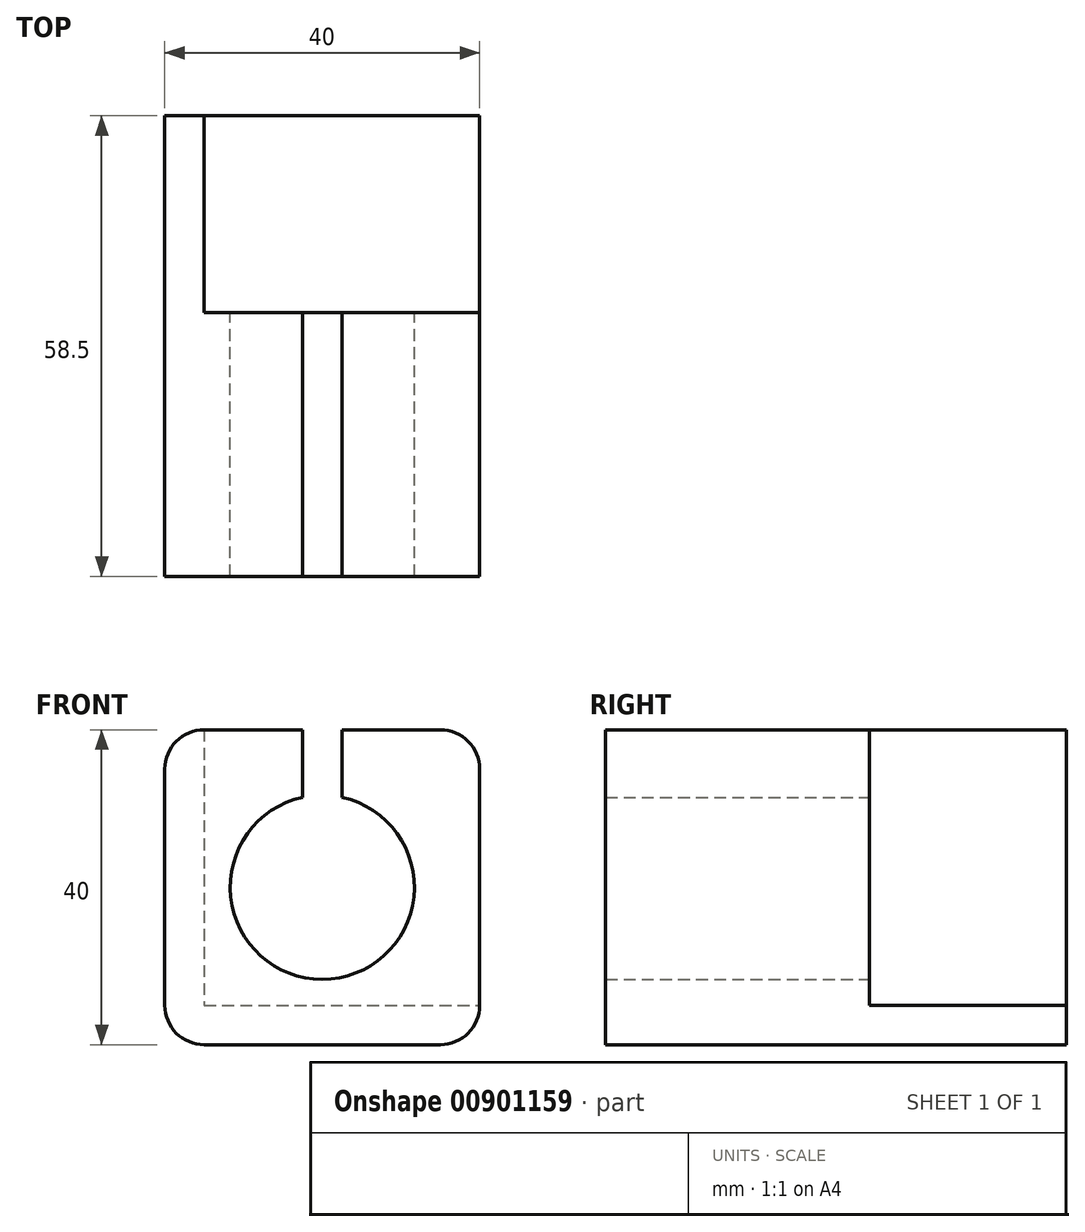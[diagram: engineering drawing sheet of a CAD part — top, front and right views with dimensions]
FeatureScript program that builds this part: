
annotation { "Feature Type Name" : "Feature", "Feature Type Description" : "" }
export const myFeature = defineFeature(function(context is Context, id is Id, definition is map)
    precondition{}
    {
        {
            var Q0;
            Q0=qCreatedBy(makeId("Front.planeOp"),FACE);
            var sketch = newSketch(context, id + "F0", { "sketchPlane" : qUnion([Q0])});
            skLineSegment(sketch, "E0.bottom", {"start": v(20, 20) * mm, "end": v(-20, 20) * mm});
            skLineSegment(sketch, "E0.top", {"start": v(20, -20) * mm, "end": v(-20, -20) * mm});
            skLineSegment(sketch, "E0.left", {"start": v(20, 20) * mm, "end": v(20, -20) * mm});
            skLineSegment(sketch, "E0.right", {"start": v(-20, 20) * mm, "end": v(-20, -20) * mm});
            skPoint(sketch, "E0.middle", {"position": v(0, 0) * mm});
            skCircle(sketch, "E1", {"center": v(0, 0) * mm, "radius": 11.7 * mm});
            skSolve(sketch);
        }
        {
            var Q0;
            Q0 = qSketchRegion(id + "F0", true);
            extrude(context, id + "F1", {"entities" : qUnion([Q0]), "depth" : 3.5 * mm, "offsetDistance" : 25 * mm});
        }
        {
            var Q0;
            Q0=makeQuery(id+"F1.opExtrude","CAP_FACE",FACE,{"disambiguationData":[OSD([sQuery(id+"F0.wireOp",EDGE,"E0.bottom"),sQuery(id+"F0.wireOp",EDGE,"E0.top"),sQuery(id+"F0.wireOp",EDGE,"E0.left"),sQuery(id+"F0.wireOp",EDGE,"E0.right"),sQuery(id+"F0.wireOp",EDGE,"E1")])],"isStart":false});
            var sketch = newSketch(context, id + "F2", { "sketchPlane" : qUnion([Q0])});
            skCircle(sketch, "E2", {"center": v(0, 0) * mm, "radius": 11.7 * mm});
            skCircle(sketch, "E3.0", {"center": v(0, 0) * mm, "radius": 16.7 * mm});
            skSolve(sketch);
        }
        {
            var Q0;
            Q0 = qSketchRegion(id + "F2", true);
            extrude(context, id + "F3", {"entities" : qUnion([Q0]), "operationType" : NewBodyOperationType.ADD, "depth" : 30 * mm, "offsetDistance" : 25 * mm});
        }
        {
            var Q0;
            Q0=makeQuery(id+"F3.opExtrude","CAP_FACE",FACE,{"disambiguationData":[OSD([sQuery(id+"F2.wireOp",EDGE,"E2"),sQuery(id+"F2.wireOp",EDGE,"E3.0")])],"isStart":false});
            var sketch = newSketch(context, id + "F4", { "sketchPlane" : qUnion([Q0])});
            skLineSegment(sketch, "E4.0", {"start": v(2.5, 0) * mm, "end": v(2.5, 29.24) * mm});
            skLineSegment(sketch, "E5.0", {"start": v(-2.5, 0) * mm, "end": v(-2.5, 29.24) * mm});
            skLineSegment(sketch, "E6", {"start": v(2.5, 29.24) * mm, "end": v(-2.5, 29.24) * mm});
            skLineSegment(sketch, "E7", {"start": v(2.5, 0) * mm, "end": v(-2.5, 0) * mm});
            skPoint(sketch, "E8.orphan", {"position": v(0, 29.24) * mm});
            skSolve(sketch);
        }
        {
            var Q0;
            Q0 = qSketchRegion(id + "F4", true);
            var Q1;
            Q1=makeQuery(id+"F1.opExtrude","CAP_FACE",FACE,{"disambiguationData":[OSD([sQuery(id+"F0.wireOp",EDGE,"E0.bottom"),sQuery(id+"F0.wireOp",EDGE,"E0.top"),sQuery(id+"F0.wireOp",EDGE,"E0.left"),sQuery(id+"F0.wireOp",EDGE,"E0.right"),sQuery(id+"F0.wireOp",EDGE,"E1")])],"isStart":false});
            extrude(context, id + "F5", {"entities" : qUnion([Q0]), "operationType" : NewBodyOperationType.REMOVE, "endBound" : BoundingType.UP_TO_NEXT, "oppositeDirection" : true, "depth" : 25 * mm, "endBoundEntityFace" : qUnion([Q1]), "offsetDistance" : 25 * mm});
        }
        {
            var Q0;
            Q0=makeQuery(id+"F3.opExtrude","CAP_FACE",FACE,{"disambiguationData":[OSD([sQuery(id+"F2.wireOp",EDGE,"E2"),sQuery(id+"F2.wireOp",EDGE,"E3.0")])],"isStart":false});
            var sketch = newSketch(context, id + "F6", { "sketchPlane" : qUnion([Q0])});
            skCircle(sketch, "E9", {"center": v(0, 0) * mm, "radius": 16.7 * mm});
            skLineSegment(sketch, "E10.bottom", {"start": v(20, 20) * mm, "end": v(-20, 20) * mm});
            skLineSegment(sketch, "E10.top", {"start": v(20, -20) * mm, "end": v(-20, -20) * mm});
            skLineSegment(sketch, "E10.left", {"start": v(20, 20) * mm, "end": v(20, -20) * mm});
            skLineSegment(sketch, "E10.right", {"start": v(-20, 20) * mm, "end": v(-20, -20) * mm});
            skSolve(sketch);
        }
        {
            var Q0;
            Q0 = qSketchRegion(id + "F6", true);
            var Q1;
            Q1=makeQuery(id+"F1.opExtrude","SWEPT_BODY",BODY,{"disambiguationData":[OSD([sQuery(id+"F0.wireOp",EDGE,"E0.bottom"),sQuery(id+"F0.wireOp",EDGE,"E0.top"),sQuery(id+"F0.wireOp",EDGE,"E0.left"),sQuery(id+"F0.wireOp",EDGE,"E0.right"),sQuery(id+"F0.wireOp",EDGE,"E1")])]});
            extrude(context, id + "F7", {"entities" : qUnion([Q0]), "operationType" : NewBodyOperationType.ADD, "oppositeDirection" : true, "depth" : 30.5 * mm, "endBoundEntityBody" : qUnion([Q1]), "offsetDistance" : 25 * mm});
        }
        {
            var Q0;
            Q0=makeQuery(id+"F7.boolean.opBoolean","MERGE",FACE,{"derivedFrom":[makeQuery(id+"F3.opExtrude","CAP_FACE",FACE,{"disambiguationData":[OSD([sQuery(id+"F2.wireOp",EDGE,"E2"),sQuery(id+"F2.wireOp",EDGE,"E3.0")])],"isStart":false}),makeQuery(id+"F7.opExtrude","CAP_FACE",FACE,{"disambiguationData":[OSD([sQuery(id+"F6.wireOp",EDGE,"E9"),sQuery(id+"F6.wireOp",EDGE,"E10.bottom"),sQuery(id+"F6.wireOp",EDGE,"E10.top"),sQuery(id+"F6.wireOp",EDGE,"E10.left"),sQuery(id+"F6.wireOp",EDGE,"E10.right")])],"isStart":true})]});
            var sketch = newSketch(context, id + "F8", { "sketchPlane" : qUnion([Q0])});
            skLineSegment(sketch, "E11", {"start": v(2.5, 11.43) * mm, "end": v(2.5, 21.55) * mm});
            skLineSegment(sketch, "E12", {"start": v(2.5, 21.55) * mm, "end": v(-2.5, 21.55) * mm});
            skLineSegment(sketch, "E13", {"start": v(-2.5, 21.55) * mm, "end": v(-2.5, 7.93) * mm});
            skLineSegment(sketch, "E14", {"start": v(-2.5, 7.93) * mm, "end": v(2.5, 7.93) * mm});
            skLineSegment(sketch, "E15", {"start": v(2.5, 7.93) * mm, "end": v(2.5, 11.43) * mm});
            skSolve(sketch);
        }
        {
            var Q0;
            Q0 = qSketchRegion(id + "F8", true);
            extrude(context, id + "F9", {"entities" : qUnion([Q0]), "operationType" : NewBodyOperationType.REMOVE, "oppositeDirection" : true, "depth" : 37.3 * mm, "offsetDistance" : 25 * mm});
        }
        {
            var Q0;
            Q0=makeQuery(id+"F1.opExtrude","CAP_FACE",FACE,{"disambiguationData":[OSD([sQuery(id+"F0.wireOp",EDGE,"E0.bottom"),sQuery(id+"F0.wireOp",EDGE,"E0.top"),sQuery(id+"F0.wireOp",EDGE,"E0.left"),sQuery(id+"F0.wireOp",EDGE,"E0.right"),sQuery(id+"F0.wireOp",EDGE,"E1")])],"isStart":true});
            var sketch = newSketch(context, id + "F10", { "sketchPlane" : qUnion([Q0])});
            skLineSegment(sketch, "E16", {"start": v(20, 20) * mm, "end": v(20, -20) * mm});
            skLineSegment(sketch, "E17", {"start": v(20, -20) * mm, "end": v(-20, -20) * mm});
            skLineSegment(sketch, "E18.0", {"start": v(15, -15) * mm, "end": v(-20, -15) * mm});
            skLineSegment(sketch, "E18.1", {"start": v(15, 20) * mm, "end": v(15, -15) * mm});
            skLineSegment(sketch, "E19", {"start": v(-20, -20) * mm, "end": v(-20, -15) * mm});
            skLineSegment(sketch, "E20", {"start": v(20, 20) * mm, "end": v(15, 20) * mm});
            skSolve(sketch);
        }
        {
            var Q0;
            Q0 = qSketchRegion(id + "F10", true);
            extrude(context, id + "F11", {"entities" : qUnion([Q0]), "operationType" : NewBodyOperationType.ADD, "depth" : 25 * mm, "offsetDistance" : 25 * mm});
        }
        {
            var Q0;
            Q0=makeQuery(id+"F11.boolean.opBoolean","MERGE",EDGE,{"derivedFrom":[makeQuery(id+"F7.boolean.opBoolean","MERGE",EDGE,{"derivedFrom":[makeQuery(id+"F1.opExtrude","SWEPT_EDGE",EDGE,{"disambiguationData":[OSD([sQuery(id+"F0.wireOp",EDGE,"E0.top"),sQuery(id+"F0.wireOp",EDGE,"E0.right")])]}),makeQuery(id+"F7.opExtrude","SWEPT_EDGE",EDGE,{"disambiguationData":[OSD([sQuery(id+"F6.wireOp",EDGE,"E10.top"),sQuery(id+"F6.wireOp",EDGE,"E10.right")])]})]}),makeQuery(id+"F11.opExtrude","SWEPT_EDGE",EDGE,{"disambiguationData":[OSD([sQuery(id+"F10.wireOp",EDGE,"E16"),sQuery(id+"F10.wireOp",EDGE,"E17")])]})]});
            var Q1;
            Q1=makeQuery(id+"F11.boolean.opBoolean","MERGE",EDGE,{"derivedFrom":[makeQuery(id+"F7.boolean.opBoolean","MERGE",EDGE,{"derivedFrom":[makeQuery(id+"F1.opExtrude","SWEPT_EDGE",EDGE,{"disambiguationData":[OSD([sQuery(id+"F0.wireOp",EDGE,"E0.bottom"),sQuery(id+"F0.wireOp",EDGE,"E0.right")])]}),makeQuery(id+"F7.opExtrude","SWEPT_EDGE",EDGE,{"disambiguationData":[OSD([sQuery(id+"F6.wireOp",EDGE,"E10.bottom"),sQuery(id+"F6.wireOp",EDGE,"E10.right")])]})]}),makeQuery(id+"F11.opExtrude","SWEPT_EDGE",EDGE,{"disambiguationData":[OSD([sQuery(id+"F10.wireOp",EDGE,"E16"),sQuery(id+"F10.wireOp",EDGE,"E20")])]})]});
            var Q2;
            Q2=makeQuery(id+"F11.boolean.opBoolean","MERGE",EDGE,{"derivedFrom":[makeQuery(id+"F7.boolean.opBoolean","MERGE",EDGE,{"derivedFrom":[makeQuery(id+"F1.opExtrude","SWEPT_EDGE",EDGE,{"disambiguationData":[OSD([sQuery(id+"F0.wireOp",EDGE,"E0.top"),sQuery(id+"F0.wireOp",EDGE,"E0.left")])]}),makeQuery(id+"F7.opExtrude","SWEPT_EDGE",EDGE,{"disambiguationData":[OSD([sQuery(id+"F6.wireOp",EDGE,"E10.top"),sQuery(id+"F6.wireOp",EDGE,"E10.left")])]})]}),makeQuery(id+"F11.opExtrude","SWEPT_EDGE",EDGE,{"disambiguationData":[OSD([sQuery(id+"F10.wireOp",EDGE,"E17"),sQuery(id+"F10.wireOp",EDGE,"E19")])]})]});
            var Q3;
            Q3=makeQuery(id+"F7.boolean.opBoolean","MERGE",EDGE,{"derivedFrom":[makeQuery(id+"F1.opExtrude","SWEPT_EDGE",EDGE,{"disambiguationData":[OSD([sQuery(id+"F0.wireOp",EDGE,"E0.bottom"),sQuery(id+"F0.wireOp",EDGE,"E0.left")])]}),makeQuery(id+"F7.opExtrude","SWEPT_EDGE",EDGE,{"disambiguationData":[OSD([sQuery(id+"F6.wireOp",EDGE,"E10.bottom"),sQuery(id+"F6.wireOp",EDGE,"E10.left")])]})]});
            fillet(context, id + "F12", {"entities" : qUnion([Q0, Q1, Q2, Q3]), "radius" : 5 * mm, "tangentPropagation" : true, "allowEdgeOverflow" : false});
        }
    });
